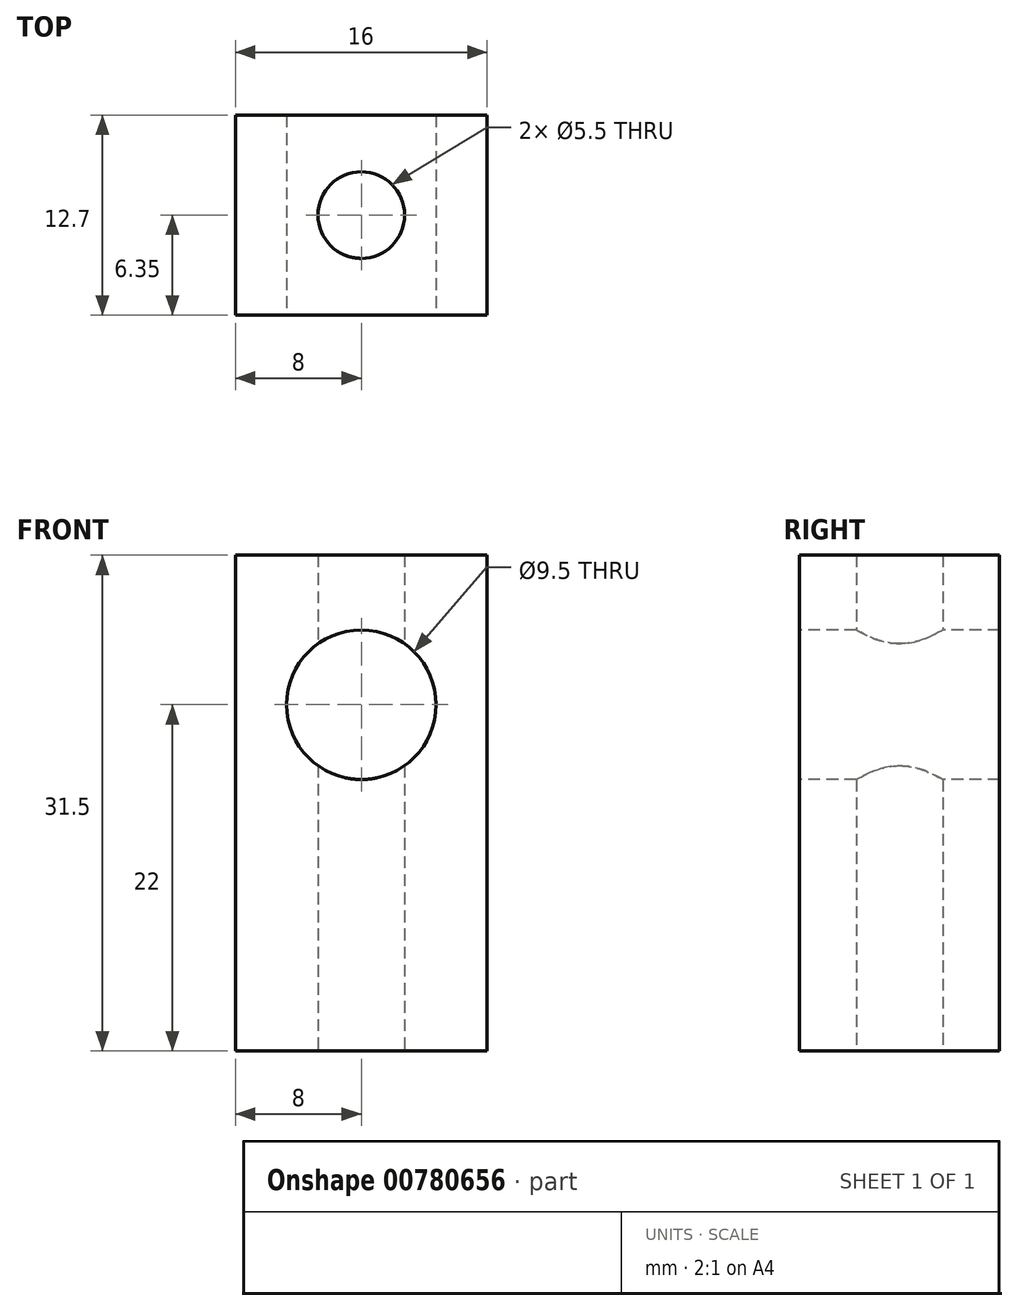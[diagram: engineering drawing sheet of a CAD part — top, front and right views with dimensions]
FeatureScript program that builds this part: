
annotation { "Feature Type Name" : "Feature", "Feature Type Description" : "" }
export const myFeature = defineFeature(function(context is Context, id is Id, definition is map)
    precondition{}
    {
        {
            var Q0;
            Q0=qCreatedBy(makeId("Front.planeOp"),FACE);
            var sketch = newSketch(context, id + "F0", { "sketchPlane" : qUnion([Q0])});
            skLineSegment(sketch, "E0.bottom", {"start": v(8, -15.75) * mm, "end": v(-8, -15.75) * mm});
            skLineSegment(sketch, "E0.top", {"start": v(8, 15.75) * mm, "end": v(-8, 15.75) * mm});
            skLineSegment(sketch, "E0.left", {"start": v(8, -15.75) * mm, "end": v(8, 15.75) * mm});
            skLineSegment(sketch, "E0.right", {"start": v(-8, -15.75) * mm, "end": v(-8, 15.75) * mm});
            skPoint(sketch, "E0.middle", {"position": v(0, 0) * mm});
            skSolve(sketch);
        }
        {
            var Q0;
            Q0 = qSketchRegion(id + "F0", true);
            extrude(context, id + "F1", {"entities" : qUnion([Q0]), "endBound" : BoundingType.SYMMETRIC, "depth" : 12.7 * mm, "offsetDistance" : 25 * mm});
        }
        {
            var Q0;
            Q0=makeQuery(id+"F1.opExtrude","CAP_FACE",FACE,{"disambiguationData":[OSD([sQuery(id+"F0.wireOp",EDGE,"E0.bottom"),sQuery(id+"F0.wireOp",EDGE,"E0.top"),sQuery(id+"F0.wireOp",EDGE,"E0.left"),sQuery(id+"F0.wireOp",EDGE,"E0.right")])],"isStart":false});
            var sketch = newSketch(context, id + "F2", { "sketchPlane" : qUnion([Q0])});
            skLineSegment(sketch, "E1", {"start": v(0, -15.75) * mm, "end": v(0, 6.25) * mm});
            skCircle(sketch, "E2", {"center": v(0, 6.25) * mm, "radius": 4.75 * mm});
            skSolve(sketch);
        }
        {
            var Q0;
            Q0 = qSketchRegion(id + "F2", true);
            extrude(context, id + "F3", {"entities" : qUnion([Q0]), "operationType" : NewBodyOperationType.REMOVE, "endBound" : BoundingType.THROUGH_ALL, "oppositeDirection" : true, "depth" : 25 * mm, "offsetDistance" : 25 * mm});
        }
        {
            var Q0;
            Q0=makeQuery(id+"F1.opExtrude","SWEPT_FACE",FACE,{"disambiguationData":[OSD([sQuery(id+"F0.wireOp",EDGE,"E0.bottom")])]});
            var sketch = newSketch(context, id + "F4", { "sketchPlane" : qUnion([Q0])});
            skCircle(sketch, "E3", {"center": v(0, 0) * mm, "radius": 2.75 * mm});
            skSolve(sketch);
        }
        {
            var Q0;
            Q0 = qSketchRegion(id + "F4", true);
            extrude(context, id + "F5", {"entities" : qUnion([Q0]), "operationType" : NewBodyOperationType.REMOVE, "endBound" : BoundingType.THROUGH_ALL, "oppositeDirection" : true, "depth" : 25 * mm, "offsetDistance" : 25 * mm});
        }
    });
